# Revit family: Deca_Cuba de quadrada de apoio_Quadratta_L.11030
name_source: partatom
category: Plumbing Fixtures
units: mm (PartAtom-declared; Revit-internal decimal feet)

## family parameters
Cut with Voids When Loaded = No
Host = Face
Part Type = Normal
Room Calculation Point = No
Round Connector Dimension = Use Radius
Shared = No

## types (2) — shared parameters
Aprovado por = quattroD
Atendimento ao Cliente = 0800-0117073
Categoria = Cubas
Composição Anel Vedação = -
Composição Assento = -
Composição Básica = Argila; feldspato; caulim; vidrados e corantes inorgânicos.
Composição Componente = Aço inoxidável; elastômeros e plásticos de engenharia.
Consumo = -
Cor Secundária = -
Cores Componente = -
Criado por = quattroD
Código Pai = L.11030
Diâmetro Ponto de Esgoto = 25 mm  [stored 0.082021 ft]
Informações Complementares = -
Itens de Instalação = -
Linha = Quadratta
Manufacturer = Deca
Norma = NBR-16728-1;NBR-16728-2
Pressão máx. funcionamento = -
Pressão mín. Aquec. Acúmulo = -
Pressão mín. Aquec. Passagem = -
Pressão mín. funcionamento = -
Raio Ponto de Esgoto = 13 mm  [stored 0.0426509 ft]
Saída de Esgoto = Válvula Curta
Segmento = Banheiro Luxo
Tipo de dispositivo economizador = -
Tipo de mecanismo utilizado = -
Tipo de rosca de entrada = -
Tipo de rosca de saída = -
URL = www.deca.com.br
Vazão na Pressão máx. (L/min) = -
Vazão na Pressão mín. (L/min) = -
zero-valued in all types: Default Elevation

## per-type parameters (varying)
| type | Acompanha o Produto | Cor Interna | Cor Principal | Description | Material | Model | Peso Líquido (Kg) |
| L.11030.17_Branco | Retentor Válvula 7701165 ; Folheto cuba squarcle 7920266 ; Tampão Cerâmico para válvula de cozinha (v.15.17.cla); | 17 - Branco | 17 - Branco | CUBA QUADRADA DE APOIO 30 CM - BRANCO | Deca_Branco | L.11030.17 | 7201 |
| L.11030.94_Ébano | Retentor Válvula 7701165 ; Folheto cuba squarcle 7920271 ; Tampão Cerâmico para válvula de cozinha (v.15.17.cla); | 94 - Ébano Fosco | 94 - Ébano Fosco | CUBA QUADRADA DE APOIO 30 CM - ÉBANO FOSCO | Deca_Ébano | L.11030.94 | 7045 |

note: [stored X ft] marks values corroborated as IEEE doubles in the binary element streams (Revit-internal decimal feet)

## geometry (parser evidence)
native form markers: Sweep x3
no freeform markers — native parametric forms only
